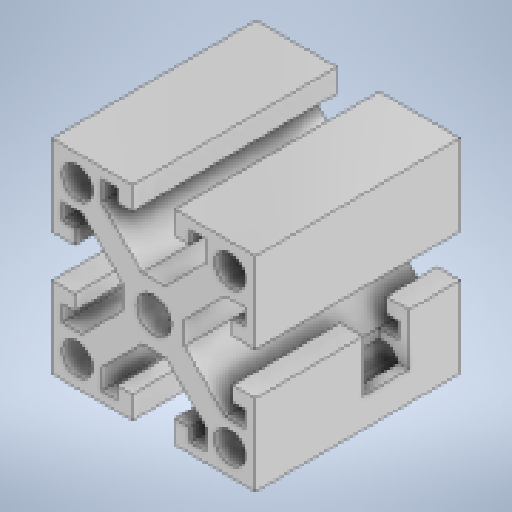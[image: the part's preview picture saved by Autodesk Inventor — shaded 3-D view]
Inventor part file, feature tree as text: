
AUTODESK INVENTOR PART (.ipt)
format: ipt  version: 2024.1 (Build 281209000, 209)  size: 337,408 bytes
history: native  units: in
note: dims shown in document units (in); Inventor stores cm internally (conversion verified against a paired STEP export)
features: reference x5, other x3, extrude x2, sketch x2
ambient origin geometry x8: Origin, YZ Plane, XZ Plane, XY Plane, X Axis, Y Axis, Z Axis, Center Point
bodies: Solid1 (feature_tree)
feature tree (12):
  extrude  "Extrusion1"  TaperAngle=45.0deg  [1 undecoded]
  extrude  "Extrusion2"  Depth=0.2362in
  sketch  "Sketch1"  dims[d0=0.2677in d1=45.0deg]
  sketch  "Sketch2"  dims[d2=0.7874in d3=0.2362in d4=0.5906in d5=0.4035in d6=0.2795in d7=0.1634in d8=0.1772in d9=0.0787in d10=0.5492in d11=0.2362in d12=1.5748in d14=360.0deg d16=1.5787in d17=0.0in d18=0.0108in d19=0.2362in d20=0.0in]
  reference  "Reference1"
  reference  "Reference2"
  reference  "Reference3"
  reference  "Reference4"
  reference  "Reference5"
  other  "1_Base.iam"
  other  "HTD-45H:1"
  other  "Aluminum_Profile_4040_40.10mm_right:1"
note: 1 required parameter value undecoded (feature->parameter linkage not recoverable at this tier; creation-order binding heuristic only, values carry confidence <= 0.55)
